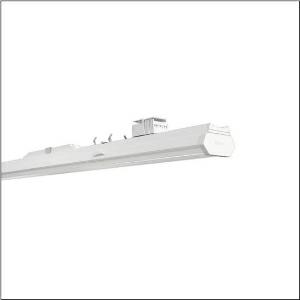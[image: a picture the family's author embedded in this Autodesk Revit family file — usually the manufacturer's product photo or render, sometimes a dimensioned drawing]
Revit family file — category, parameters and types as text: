
# Revit family: licross_r__21_protected_ho_52td11dn4dxs_f76a
name_source: partatom
category: Lighting Fixtures
units: mm (PartAtom-declared; Revit-internal decimal feet)

## family parameters
Cut with Voids When Loaded = No
Host = Face
Light Source = No
Part Type = Normal
Room Calculation Point = No
Round Connector Dimension = Use Diameter
Shared = No

## types (1)
- --- (1 x LED, 13000 lm, 73.1 W, 4000K)
    Apparent Load = 73 VA
    CIE Flux Codes = 84 94 98 99 100
    Color Rendering = 80
    Color Temperature = 4000K
    Default Elevation = 1800 mm
    Description = Licross® 21 Protected HO, luminaire insert, of sheet steel, galvanised, coil coated, white, length: 1.500mm, width: 90mm, height: 103mm, LED rated luminous flux: 13.000lm, light colour: 840, control gear: DALI 2, with plug, 5-pole, with phase selection, mains connection: 220..240V, AC, 50/60Hz, rated input power: 73W, internal wiring halogen-free, primary light control with lens, of plastic, primary optical cover: cover, of PMMA, light emission: direct distribution, primary light characteristic: symmetric, protection rating (complete): IP54, insulation class (complete): insulation class I (protective earthing), certification: CE, ENEC, VDE, UKCA, protection symbol: D if used in an environment with non-conductive dust loads with corresponding accessories, impact resistance: IK06, permissible ambient temperature for indoor applications: -25..+40°C, corresponds to IFS (International Featured Standards) requirements for safety and quality in the food industry, reducing of maximum allowable ambient temperature of 5°C with ceiling mounting, LABS conformity tested according to VDMA 24364:2018-05, packaging unit: 1 piece
    Height = 92 mm
    Lamp = 1 x LED
    Lamp Light Flux = 13000 lm
    Lamp Power = 73.1 W
    Lamp count = 1
    Length = 1500 mm
    Luminous efficacy = 178 lm/W
    Manufacturer = Siteco
    ModVariant = No
    Model = 52TD11DN4DXS
    Mounting Place = Ceiling
    Mounting Type = Pendant
    Number of Poles = 1
    OnlyDefault = Yes
    Power Factor = 1
    Product Name = Licross® 21 Protected HO
    Product group = luminaire insert | ceiling pendant
    ProductGroupID = 902
    Protection Class = Protection class I
    Protection Degree = IP 54
    RLX_Detail_Level = 1
    RLX_Emergency_Light_Flux = 0 lm
    RLX_Emergency_Type = 0
    RLX_Emergency_Type_DB = No
    RlxData = <blob elided: 24373 chars, md5=afd78bbf>
    Socket = socket
    Standby Power = 0 W
    System Light Flux = 13000 lm
    System Power = 73 W
    Type Comments = factory setting: luminous flux: 100 % | dim-lin: 254 | 417 mA
    Type Image = l_1256148.jpg
    URL = http://relux.com
    VarID = @adj_149987
    Voltage = 0 V
    Weight = 0.00 kg
    Width = 88 mm

## geometry (parser evidence)
native form markers: Blend x4, Sweep x10
no freeform markers — native parametric forms only
